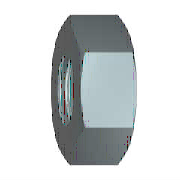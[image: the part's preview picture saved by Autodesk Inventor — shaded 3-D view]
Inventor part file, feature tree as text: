
AUTODESK INVENTOR PART (.ipt)
format: ipt  version: 2023.2 (Build 272271030, 271C)  size: 172,032 bytes
history: native  units: mm (DEFAULTED — no unit token found)
features: sketch x3, chamfer x1, hole x1, other x1, plane x1
ambient origin geometry x7: Origin, YZ Plane, XZ Plane, X Axis, Y Axis, Z Axis, Center Point
bodies: Solid1 (feature_tree), Body (feature_tree)
feature tree (7):
  chamfer  "Chamfer1"  Angle=30.0deg  [1 undecoded]
  hole  "Thread"  [1 undecoded]
  other  "Work Axis1"
  plane  "Work Plane1"
  sketch  "Sketch1"  dims[d0=20.78461mm]
  sketch  "Sketch2"  dims[d1=12.0mm]
  sketch  "Sketch3"  dims[d2=0.0mm d3=30.0deg d4=30.0deg d5=18.0mm d6=18.0mm d7=90.0deg d25=10.106mm d26=6.0mm d27=4.0mm d28=2.0mm d29=14.3117mm d30=8.0mm d31=20.594885mm d8=0.947215mm d9=30.0deg d10=0.947215mm d11=30.0deg d13=0.0mm d14=0.0mm d39=0.0mm d40=0.947215mm d41=0.947215mm d42=0.0mm]
note: 2 required parameter values undecoded (feature->parameter linkage not recoverable at this tier; creation-order binding heuristic only, values carry confidence <= 0.55)
